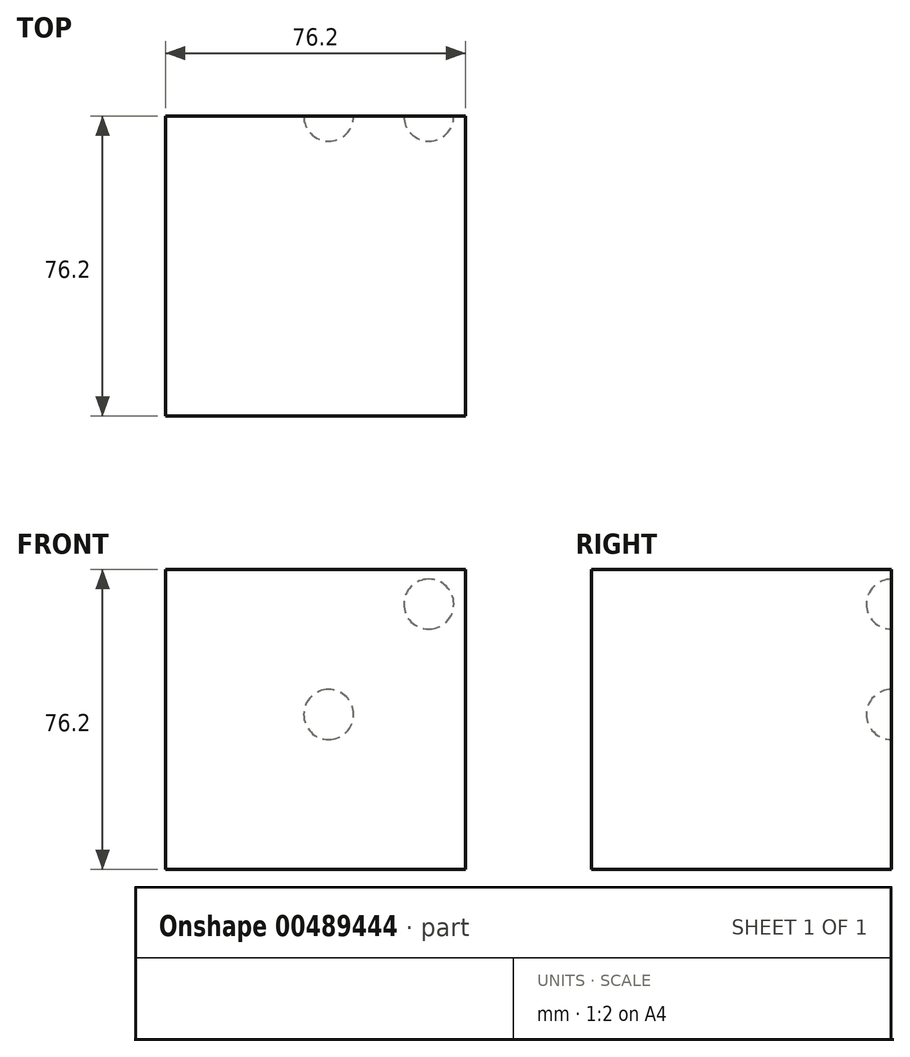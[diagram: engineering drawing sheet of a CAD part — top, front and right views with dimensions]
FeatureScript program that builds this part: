
annotation { "Feature Type Name" : "Feature", "Feature Type Description" : "" }
export const myFeature = defineFeature(function(context is Context, id is Id, definition is map)
    precondition{}
    {
        {
            var Q0;
            Q0=qCreatedBy(makeId("Front.planeOp"),FACE);
            var sketch = newSketch(context, id + "F0", { "sketchPlane" : qUnion([Q0])});
            skLineSegment(sketch, "E0", {"start": v(0, 0) * mm, "end": v(0, 76.2) * mm});
            skLineSegment(sketch, "E1", {"start": v(0, 76.2) * mm, "end": v(76.2, 76.2) * mm});
            skLineSegment(sketch, "E2", {"start": v(76.2, 76.2) * mm, "end": v(76.2, 0) * mm});
            skLineSegment(sketch, "E3", {"start": v(76.2, 0) * mm, "end": v(0, 0) * mm});
            skSolve(sketch);
        }
        {
            var Q0;
            Q0=makeQuery(id+"F0.imprint","IMPRINT",FACE,{"disambiguationData":[TD([[makeQuery(id+"F0.imprint","IMPRINT",EDGE,{"derivedFrom":sQuery(id+"F0.wireOp",EDGE,"E0")}),-1.0]])]});
            extrude(context, id + "F1", {"entities" : qUnion([Q0]), "depth" : 76.2 * mm});
        }
        {
            var Q0;
            Q0=makeQuery(id+"F0.imprint","IMPRINT",FACE,{"disambiguationData":[TD([[makeQuery(id+"F0.imprint","IMPRINT",EDGE,{"derivedFrom":sQuery(id+"F0.wireOp",EDGE,"E0")}),-1.0]])]});
            var sketch = newSketch(context, id + "F2", { "sketchPlane" : qUnion([Q0])});
            skArc(sketch, "E4", {"start": v(66.87, 61.05) * mm, "mid": v(73.22, 67.4) * mm, "end": v(66.87, 73.75) * mm});
            skLineSegment(sketch, "E5", {"start": v(66.87, 77.28) * mm, "end": v(66.87, 0) * mm});
            skLineSegment(sketch, "E6", {"start": v(37.37, 38.78) * mm, "end": v(10.95, 10.9) * mm});
            skSolve(sketch);
        }
        {
            var Q0;
            Q0 = qSketchRegion(id + "F2", true);
            var Q1;
            Q1=sQuery(id+"F2.wireOp",EDGE,"E5");
            revolve(context, id + "F3", {"operationType" : NewBodyOperationType.REMOVE, "entities" : qUnion([Q0]), "axis" : qUnion([Q1]), "revolveType" : RevolveType.FULL, "oppositeDirection" : true});
        }
        {
            var Q0;
            Q0=makeQuery(id+"F0.imprint","IMPRINT",FACE,{"disambiguationData":[TD([[makeQuery(id+"F0.imprint","IMPRINT",EDGE,{"derivedFrom":sQuery(id+"F0.wireOp",EDGE,"E0")}),-1.0]])]});
            var sketch = newSketch(context, id + "F4", { "sketchPlane" : qUnion([Q0])});
            skPoint(sketch, "E7.orphan", {"position": v(0, 42.83) * mm});
            skArc(sketch, "E8", {"start": v(41.43, 33.01) * mm, "mid": v(47.78, 39.36) * mm, "end": v(41.43, 45.71) * mm});
            skPoint(sketch, "E9.orphan", {"position": v(82.87, 39.36) * mm});
            skPoint(sketch, "E10.orphan", {"position": v(0, 39.36) * mm});
            skPoint(sketch, "E11.orphan", {"position": v(46.22, 0) * mm});
            skLineSegment(sketch, "E12", {"start": v(41.43, 76.54) * mm, "end": v(41.43, -2.1) * mm});
            skSolve(sketch);
        }
        {
            var Q0;
            Q0 = qSketchRegion(id + "F4", true);
            var Q1;
            Q1=sQuery(id+"F4.wireOp",EDGE,"E12");
            revolve(context, id + "F5", {"operationType" : NewBodyOperationType.REMOVE, "entities" : qUnion([Q0]), "axis" : qUnion([Q1]), "revolveType" : RevolveType.FULL, "oppositeDirection" : true});
        }
    });
